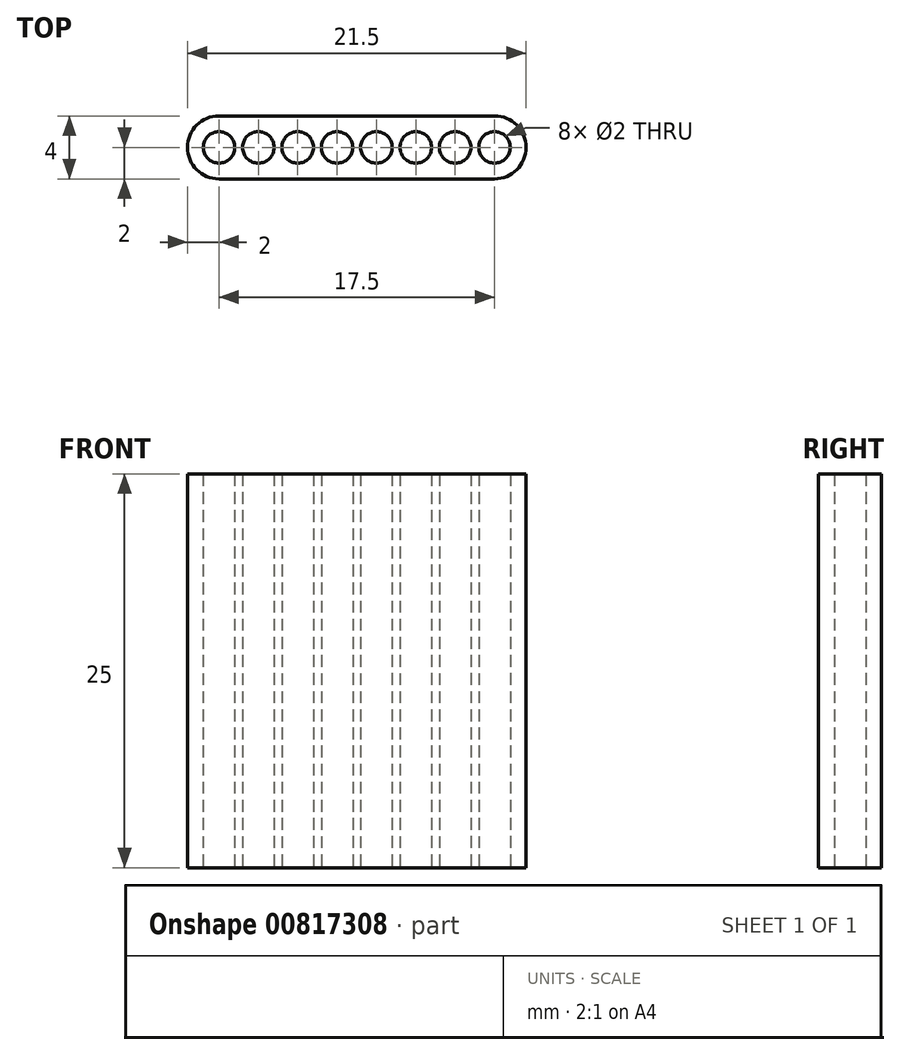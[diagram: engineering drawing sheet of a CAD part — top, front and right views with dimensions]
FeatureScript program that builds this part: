
annotation { "Feature Type Name" : "Feature", "Feature Type Description" : "" }
export const myFeature = defineFeature(function(context is Context, id is Id, definition is map)
    precondition{}
    {
        {
            var Q0;
            Q0=qCreatedBy(makeId("Top.planeOp"),FACE);
            var sketch = newSketch(context, id + "F0", { "sketchPlane" : qUnion([Q0])});
            skPoint(sketch, "E0", {"position": v(0, 9.6) * mm});
            skPoint(sketch, "E1.1.0.0", {"position": v(2.5, 9.6) * mm});
            skPoint(sketch, "E1.2.0.0", {"position": v(5, 9.6) * mm});
            skPoint(sketch, "E1.3.0.0", {"position": v(7.5, 9.6) * mm});
            skPoint(sketch, "E1.4.0.0", {"position": v(10, 9.6) * mm});
            skPoint(sketch, "E1.5.0.0", {"position": v(12.5, 9.6) * mm});
            skPoint(sketch, "E1.6.0.0", {"position": v(15, 9.6) * mm});
            skPoint(sketch, "E1.7.0.0", {"position": v(17.5, 9.6) * mm});
            skLineSegment(sketch, "E1.direction1", {"start": v(0, 9.6) * mm, "end": v(2.5, 9.6) * mm, "construction": true});
            skLineSegment(sketch, "E2", {"start": v(0, 7.6) * mm, "end": v(17.5, 7.6) * mm});
            skLineSegment(sketch, "E3", {"start": v(0, 11.6) * mm, "end": v(17.5, 11.6) * mm});
            skPoint(sketch, "E4", {"position": v(17.5, 11.6) * mm});
            skArc(sketch, "E5", {"start": v(0, 11.6) * mm, "mid": v(-2, 9.6) * mm, "end": v(0, 7.6) * mm});
            skArc(sketch, "E6", {"start": v(17.5, 11.6) * mm, "mid": v(19.5, 9.6) * mm, "end": v(17.5, 7.6) * mm});
            skSolve(sketch);
        }
        {
            var Q0;
            Q0 = qSketchRegion(id + "F0", true);
            extrude(context, id + "F1", {"entities" : qUnion([Q0]), "depth" : 25 * mm, "offsetDistance" : 25 * mm});
        }
        {
            var Q0;
            Q0=sQuery(id+"F0.wireOp",VERTEX,"E0");
            var Q1;
            Q1=sQuery(id+"F0.wireOp",VERTEX,"E1.1.0.0");
            var Q2;
            Q2=sQuery(id+"F0.wireOp",VERTEX,"E1.2.0.0");
            var Q3;
            Q3=sQuery(id+"F0.wireOp",VERTEX,"E1.3.0.0");
            var Q4;
            Q4=sQuery(id+"F0.wireOp",VERTEX,"E1.4.0.0");
            var Q5;
            Q5=sQuery(id+"F0.wireOp",VERTEX,"E1.5.0.0");
            var Q6;
            Q6=sQuery(id+"F0.wireOp",VERTEX,"E1.6.0.0");
            var Q7;
            Q7=sQuery(id+"F0.wireOp",VERTEX,"E1.7.0.0");
            var Q8;
            Q8=makeQuery(id+"F1.opExtrude","SWEPT_BODY",BODY,{"disambiguationData":[OSD([sQuery(id+"F0.wireOp",EDGE,"E2"),sQuery(id+"F0.wireOp",EDGE,"E3"),sQuery(id+"F0.wireOp",EDGE,"ZizPKiRM-KmKs-KONQ-UI5w-YsYPWrer1I0L"),sQuery(id+"F0.wireOp",EDGE,"Mq3zGvjS-doHS-SRtS-Hxbb-VXJnTxUGf3xW")])]});
            hole(context, id + "F2", {"style" : HoleStyle.SIMPLE, "endStyle" : HoleEndStyle.THROUGH, "oppositeDirection" : true, "holeDiameter" : 2 * mm, "majorDiameter" : 5 * mm, "isTappedThrough" : true, "tappedDepth" : 12 * mm, "tapClearance" : 3, "locations" : qUnion([Q0, Q1, Q2, Q3, Q4, Q5, Q6, Q7]), "scope" : qUnion([Q8])});
        }
    });
